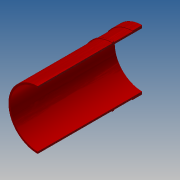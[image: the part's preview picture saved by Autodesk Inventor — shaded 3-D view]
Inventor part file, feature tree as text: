
AUTODESK INVENTOR PART (.ipt)
format: ipt  version: 2017.3 (Build 213257000, 257)  size: 149,504 bytes
history: native  units: in
note: dims shown in document units (in); Inventor stores cm internally (conversion verified against a paired STEP export)
features: other x3, extrude x3, sketch x3, plane x1, projected_geometry x1
ambient origin geometry x8: Origin, YZ Plane, XZ Plane, XY Plane, X Axis, Y Axis, Z Axis, Center Point
bodies: Solid1 (feature_tree)
feature tree (11):
  other  "A1-19027-300-04 HCWI liner - nozzle.ipt"
  extrude  "Extrusion1"  Depth=0.3937in
  plane  "Work Plane1"
  extrude  "Extrusion2"  [1 undecoded]
  extrude  "Extrusion3"  Depth=0.5in TaperAngle=0.0deg
  other  "Solid1::A1-19027-300-04 HCWI liner - nozzle.ipt"
  other  "TaggingFeature1"
  sketch  "Sketch2"  dims[d0=0.3937in d1=0.25in]
  sketch  "Sketch3"  dims[d2=0.5in d3=4.5in d4=0.0in d5=0.0in d6=-15.5394in]
  projected_geometry  "Projected Loop1"
  sketch  "Sketch4"  dims[d7=1.0in d8=0.0in d9=0.5in d10=0.5in d11=0.0in d12=0.0in]
note: 1 required parameter value undecoded (feature->parameter linkage not recoverable at this tier; creation-order binding heuristic only, values carry confidence <= 0.55)
